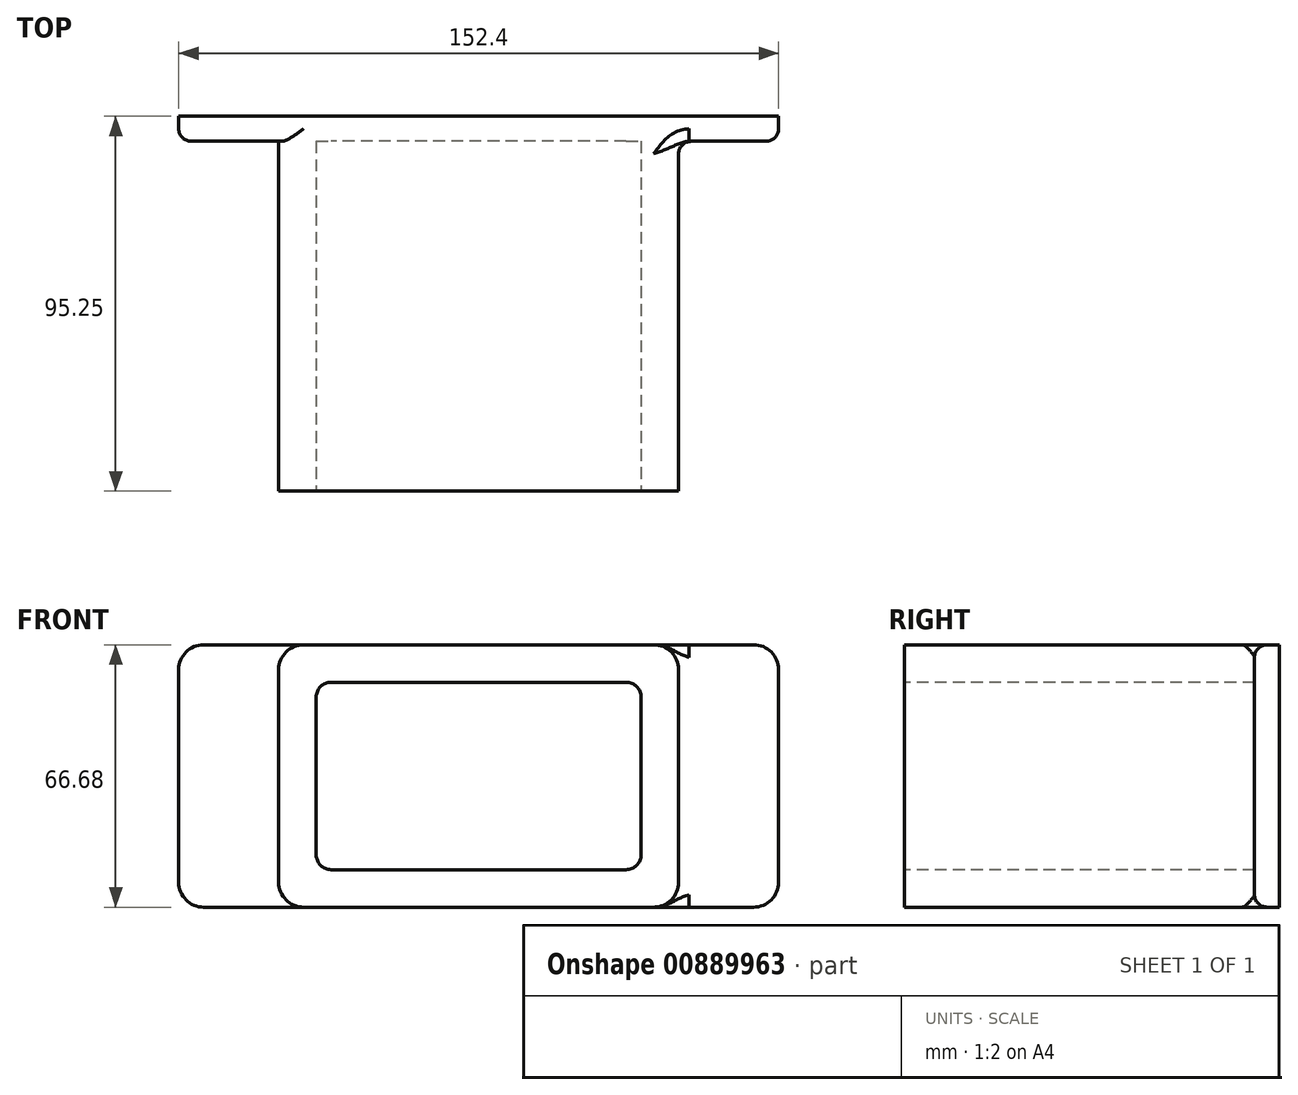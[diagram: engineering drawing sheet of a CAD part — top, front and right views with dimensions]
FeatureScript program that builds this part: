
annotation { "Feature Type Name" : "Feature", "Feature Type Description" : "" }
export const myFeature = defineFeature(function(context is Context, id is Id, definition is map)
    precondition{}
    {
        {
            var Q0;
            Q0=qCreatedBy(makeId("Front.planeOp"),FACE);
            var sketch = newSketch(context, id + "F0", { "sketchPlane" : qUnion([Q0])});
            skLineSegment(sketch, "E0.bottom", {"start": v(76.2, 33.34) * mm, "end": v(-76.2, 33.34) * mm});
            skLineSegment(sketch, "E0.top", {"start": v(76.2, -33.34) * mm, "end": v(-76.2, -33.34) * mm});
            skLineSegment(sketch, "E0.left", {"start": v(76.2, 33.34) * mm, "end": v(76.2, -33.34) * mm});
            skLineSegment(sketch, "E0.right", {"start": v(-76.2, 33.34) * mm, "end": v(-76.2, -33.34) * mm});
            skPoint(sketch, "E0.middle", {"position": v(0, 0) * mm});
            skSolve(sketch);
        }
        {
            var Q0;
            Q0 = qSketchRegion(id + "F0", true);
            extrude(context, id + "F1", {"entities" : qUnion([Q0]), "depth" : 6.35 * mm, "offsetDistance" : 25.4 * mm});
        }
        {
            var Q0;
            Q0=makeQuery(id+"F1.opExtrude","CAP_FACE",FACE,{"disambiguationData":[OSD([sQuery(id+"F0.wireOp",EDGE,"E0.bottom"),sQuery(id+"F0.wireOp",EDGE,"E0.top"),sQuery(id+"F0.wireOp",EDGE,"E0.left"),sQuery(id+"F0.wireOp",EDGE,"E0.right")])],"isStart":false});
            var sketch = newSketch(context, id + "F2", { "sketchPlane" : qUnion([Q0])});
            skLineSegment(sketch, "E1.bottom", {"start": v(50.8, 33.34) * mm, "end": v(-50.8, 33.34) * mm});
            skLineSegment(sketch, "E1.top", {"start": v(50.8, -33.34) * mm, "end": v(-50.8, -33.34) * mm});
            skLineSegment(sketch, "E1.left", {"start": v(50.8, 33.34) * mm, "end": v(50.8, -33.34) * mm});
            skLineSegment(sketch, "E1.right", {"start": v(-50.8, 33.34) * mm, "end": v(-50.8, -33.34) * mm});
            skPoint(sketch, "E1.middle", {"position": v(0, 0) * mm});
            skSolve(sketch);
        }
        {
            var Q0;
            Q0 = qSketchRegion(id + "F2", true);
            extrude(context, id + "F3", {"entities" : qUnion([Q0]), "operationType" : NewBodyOperationType.ADD, "depth" : 88.9 * mm, "offsetDistance" : 25.4 * mm});
        }
        {
            var Q0;
            Q0=makeQuery(id+"F3.opExtrude","SWEPT_EDGE",EDGE,{"disambiguationData":[OSD([sQuery(id+"F0.wireOp",EDGE,"E0.bottom"),sQuery(id+"F2.wireOp",EDGE,"E1.bottom"),sQuery(id+"F2.wireOp",EDGE,"E1.left")])]});
            var Q1;
            Q1=makeQuery(id+"F3.opExtrude","SWEPT_EDGE",EDGE,{"disambiguationData":[OSD([sQuery(id+"F0.wireOp",EDGE,"E0.top"),sQuery(id+"F2.wireOp",EDGE,"E1.top"),sQuery(id+"F2.wireOp",EDGE,"E1.left")])]});
            var Q2;
            Q2=makeQuery(id+"F3.opExtrude","SWEPT_EDGE",EDGE,{"disambiguationData":[OSD([sQuery(id+"F0.wireOp",EDGE,"E0.bottom"),sQuery(id+"F2.wireOp",EDGE,"E1.bottom"),sQuery(id+"F2.wireOp",EDGE,"E1.right")])]});
            var Q3;
            Q3=makeQuery(id+"F3.opExtrude","SWEPT_EDGE",EDGE,{"disambiguationData":[OSD([sQuery(id+"F0.wireOp",EDGE,"E0.top"),sQuery(id+"F2.wireOp",EDGE,"E1.top"),sQuery(id+"F2.wireOp",EDGE,"E1.right")])]});
            var Q4;
            Q4=makeQuery(id+"F1.opExtrude","SWEPT_EDGE",EDGE,{"disambiguationData":[OSD([sQuery(id+"F0.wireOp",EDGE,"E0.bottom"),sQuery(id+"F0.wireOp",EDGE,"E0.right")])]});
            var Q5;
            Q5=makeQuery(id+"F1.opExtrude","SWEPT_EDGE",EDGE,{"disambiguationData":[OSD([sQuery(id+"F0.wireOp",EDGE,"E0.top"),sQuery(id+"F0.wireOp",EDGE,"E0.right")])]});
            var Q6;
            Q6=makeQuery(id+"F1.opExtrude","SWEPT_EDGE",EDGE,{"disambiguationData":[OSD([sQuery(id+"F0.wireOp",EDGE,"E0.top"),sQuery(id+"F0.wireOp",EDGE,"E0.left")])]});
            var Q7;
            Q7=makeQuery(id+"F1.opExtrude","SWEPT_EDGE",EDGE,{"disambiguationData":[OSD([sQuery(id+"F0.wireOp",EDGE,"E0.bottom"),sQuery(id+"F0.wireOp",EDGE,"E0.left")])]});
            fillet(context, id + "F4", {"entities" : qUnion([Q0, Q1, Q2, Q3, Q4, Q5, Q6, Q7]), "radius" : 6.35 * mm, "tangentPropagation" : true, "allowEdgeOverflow" : false});
        }
        {
            var Q0;
            Q0=makeQuery(id+"F1.opExtrude","CAP_EDGE",EDGE,{"disambiguationData":[OSD([sQuery(id+"F0.wireOp",EDGE,"E0.left")])],"isStart":false});
            var Q1;
            Q1=makeQuery(id+"F3.opExtrude","CAP_EDGE",EDGE,{"disambiguationData":[OSD([sQuery(id+"F2.wireOp",EDGE,"E1.right")])],"isStart":true});
            var Q2;
            Q2=makeQuery(id+"F1.opExtrude","CAP_EDGE",EDGE,{"disambiguationData":[OSD([sQuery(id+"F0.wireOp",EDGE,"E0.right")])],"isStart":false});
            var Q3;
            Q3=makeQuery(id+"F3.opExtrude","CAP_EDGE",EDGE,{"disambiguationData":[OSD([sQuery(id+"F2.wireOp",EDGE,"E1.left")])],"isStart":true});
            fillet(context, id + "F5", {"entities" : qUnion([Q0, Q1, Q2, Q3]), "radius" : 3.17 * mm, "tangentPropagation" : true, "allowEdgeOverflow" : false});
        }
        {
            var Q0;
            Q0=makeQuery(id+"F3.opExtrude","CAP_FACE",FACE,{"disambiguationData":[OSD([sQuery(id+"F2.wireOp",EDGE,"E1.bottom"),sQuery(id+"F2.wireOp",EDGE,"E1.top"),sQuery(id+"F2.wireOp",EDGE,"E1.left"),sQuery(id+"F2.wireOp",EDGE,"E1.right")])],"isStart":false});
            var sketch = newSketch(context, id + "F6", { "sketchPlane" : qUnion([Q0])});
            skLineSegment(sketch, "E2.bottom", {"start": v(37.47, 23.81) * mm, "end": v(-37.47, 23.81) * mm});
            skLineSegment(sketch, "E2.top", {"start": v(37.47, -23.81) * mm, "end": v(-37.47, -23.81) * mm});
            skLineSegment(sketch, "E2.left", {"start": v(41.28, 20) * mm, "end": v(41.28, -20) * mm});
            skLineSegment(sketch, "E2.right", {"start": v(-41.28, 20) * mm, "end": v(-41.28, -20) * mm});
            skPoint(sketch, "E2.middle", {"position": v(0, 0) * mm});
            skPoint(sketch, "E3.visualSharp", {"position": v(-41.28, 23.81) * mm});
            skArc(sketch, "E3.filletArc", {"start": v(-37.47, 23.81) * mm, "mid": v(-40.16, 22.7) * mm, "end": v(-41.28, 20) * mm});
            skPoint(sketch, "E4.visualSharp", {"position": v(-41.28, -23.81) * mm});
            skArc(sketch, "E4.filletArc", {"start": v(-41.28, -20) * mm, "mid": v(-40.16, -22.7) * mm, "end": v(-37.47, -23.81) * mm});
            skPoint(sketch, "E5.visualSharp", {"position": v(41.28, -23.81) * mm});
            skArc(sketch, "E5.filletArc", {"start": v(37.47, -23.81) * mm, "mid": v(40.16, -22.7) * mm, "end": v(41.28, -20) * mm});
            skPoint(sketch, "E6.visualSharp", {"position": v(41.28, 23.81) * mm});
            skArc(sketch, "E6.filletArc", {"start": v(41.28, 20) * mm, "mid": v(40.16, 22.7) * mm, "end": v(37.47, 23.81) * mm});
            skSolve(sketch);
        }
        {
            var Q0;
            Q0=makeQuery(id+"F6.imprint","IMPRINT",FACE,{"disambiguationData":[TD([[makeQuery(id+"F6.imprint","IMPRINT",EDGE,{"derivedFrom":sQuery(id+"F6.wireOp",EDGE,"E2.bottom")}),1.0]])]});
            extrude(context, id + "F7", {"entities" : qUnion([Q0]), "operationType" : NewBodyOperationType.REMOVE, "oppositeDirection" : true, "depth" : 88.9 * mm, "offsetDistance" : 25.4 * mm});
        }
    });
